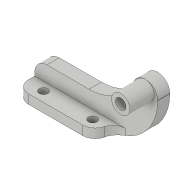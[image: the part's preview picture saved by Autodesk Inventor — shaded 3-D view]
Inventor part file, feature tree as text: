
AUTODESK INVENTOR PART (.ipt)
format: ipt  version: 2018 (Build 220112000, 112)  size: 180,224 bytes
history: native  units: in
note: dims shown in document units (in); Inventor stores cm internally (conversion verified against a paired STEP export)
features: sketch x6, fillet x5, extrude x4, hole x2, plane x1, mirror x1
ambient origin geometry x8: Origin, YZ Plane, XZ Plane, XY Plane, X Axis, Y Axis, Z Axis, Center Point
bodies: Solid1 (feature_tree)
feature tree (19):
  extrude  "Extrusion1"  Depth=0.894in
  hole  "Hole1"  [1 undecoded]
  extrude  "Extrusion2"  Depth=0.25in
  fillet  "Fillet1"  Radius=0.25in
  fillet  "Fillet2"  Radius=0.25in
  extrude  "Extrusion3"  Depth=0.25in
  fillet  "Fillet3"  Radius=1.069in
  fillet  "Fillet4"  Radius=0.5in
  hole  "Hole2"  [1 undecoded]
  fillet  "Fillet5"  Radius=0.644in
  plane  "Work Plane1"
  mirror  "Mirror1"
  extrude  "Extrusion4"  Depth=0.1875in
  sketch  "Sketch1"  dims[d0=2.5in d2=0.894in]
  sketch  "Sketch2"  dims[d3=1.0in d4=1.069in]
  sketch  "Sketch3"  dims[d5=0.0in d6=0.25in d7=0.25in d8=0.25in d9=0.0in]
  sketch  "Sketch4"  dims[d10=0.25in d11=0.25in d12=1.069in]
  sketch  "Sketch5"  dims[d13=0.2165in d14=0.75in d15=0.375in d16=0.25in d17=0.5635in d18=1.0in d19=0.8108in d20=0.5in d21=0.0in]
  sketch  "Sketch6"  dims[d22=0.25in d23=1.0in d24=0.644in d25=0.1875in d26=0.375in d27=0.0in d28=0.25in d29=0.25in d30=1.0in d31=0.894in d32=0.177in d33=0.75in d34=0.332in d35=0.25in d36=0.5635in d37=1.0in d38=0.8108in d39=0.25in d40=1.0in d41=4.0in d42=0.0in]
note: 2 required parameter values undecoded (feature->parameter linkage not recoverable at this tier; creation-order binding heuristic only, values carry confidence <= 0.55)
